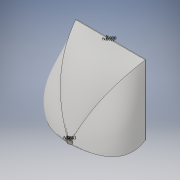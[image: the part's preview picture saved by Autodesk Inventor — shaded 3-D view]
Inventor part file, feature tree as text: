
AUTODESK INVENTOR PART (.ipt)
format: ipt  version: 2017 (Build 210142000, 142)  size: 372,224 bytes
history: native  units: in
note: dims shown in document units (in); Inventor stores cm internally (conversion verified against a paired STEP export)
features: sketch x8, extrude x2, plane x2, loft x2
ambient origin geometry x8: Origin, YZ Plane, XZ Plane, XY Plane, X Axis, Y Axis, Z Axis, Center Point
bodies: Solid1 (feature_tree)
feature tree (14):
  extrude  "Extrusion1"  Depth=1.0in TaperAngle=0.0deg
  sketch  "Sketch4"  dims[d26=69.0in d27=59.0in]
  plane  "Work Plane1"
  sketch  "Sketch2"  dims[d14=30.0in d15=70.0in]
  plane  "Work Plane2"
  sketch  "Sketch3"  dims[d16=60.0in d17=30.0in]
  loft  "shell make "
  loft  "shell cut"
  extrude  "Extrusion2"  Depth=59.0in
  sketch  "Sketch6"  dims[d29=102.0in]
  sketch  "Sketch7"  dims[d33=1.0in]
  sketch  "Sketch9"  dims[d34=1.0in d35=1.0in d36=1.0in d43=0.0in d44=90.0deg d45=0.0in d46=90.0deg d47=0.0in d48=90.0deg d49=0.0in d50=90.0deg d51=0.0in d52=90.0deg d53=0.0in d54=90.0deg d55=100.0in d56=100.0in d57=1.0in d58=0.0in d59=0.5833in d60=0.0625in d61=0.0625in d62=0.125in d71=7.0in d72=0.0625in d73=0.0625in d74=0.125in]
  sketch  "Sketch1"  dims[d0=4.0in d1=1.0in d2=4.8944in d4=3.8873in d5=3.8873in d12=1.0in d13=0.0in]
  sketch  "Sketch5"  dims[d28=102.0in]
